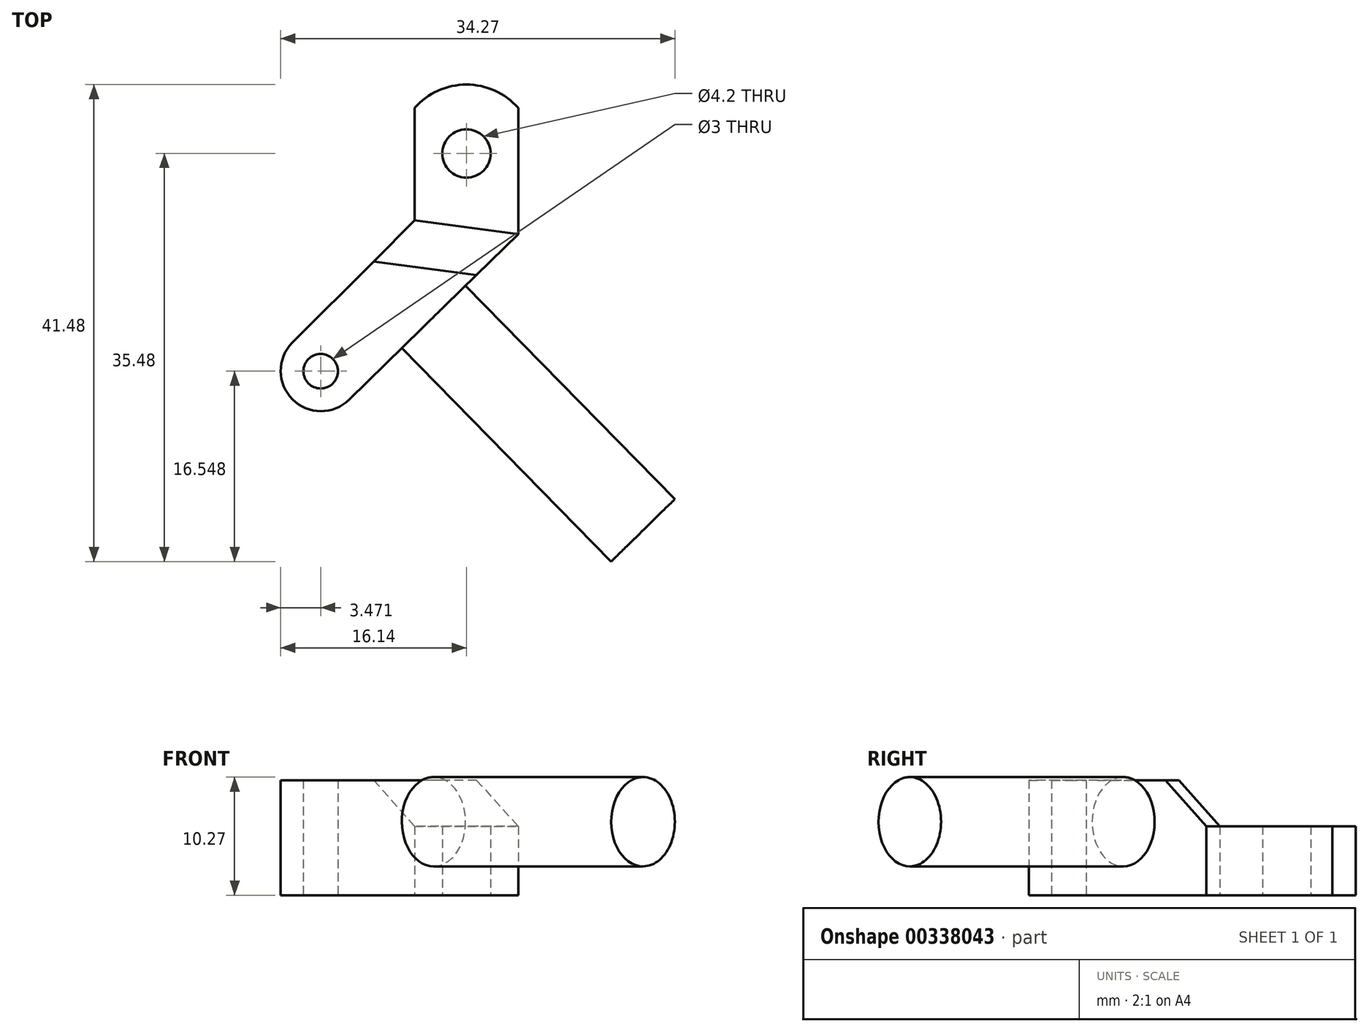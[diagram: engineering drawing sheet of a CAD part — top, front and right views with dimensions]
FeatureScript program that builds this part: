
annotation { "Feature Type Name" : "Feature", "Feature Type Description" : "" }
export const myFeature = defineFeature(function(context is Context, id is Id, definition is map)
    precondition{}
    {
        {
            var Q0;
            Q0=qCreatedBy(makeId("Top.planeOp"),FACE);
            var sketch = newSketch(context, id + "F0", { "sketchPlane" : qUnion([Q0])});
            skPoint(sketch, "E0.middle", {"position": v(0, 0) * mm});
            skCircle(sketch, "E1", {"center": v(0, 0) * mm, "radius": 2.1 * mm});
            skArc(sketch, "E2", {"start": v(4.5, 3.97) * mm, "mid": v(0, 6) * mm, "end": v(-4.5, 3.97) * mm});
            skLineSegment(sketch, "E3", {"start": v(4.5, 0) * mm, "end": v(4.5, 3.97) * mm});
            skLineSegment(sketch, "E4", {"start": v(0, 14.22) * mm, "end": v(0, -15.58) * mm, "construction": true});
            skLineSegment(sketch, "E5.MirrorCS", {"start": v(-4.5, 0) * mm, "end": v(-4.5, 3.97) * mm});
            skLineSegment(sketch, "E6", {"start": v(-4.5, 0) * mm, "end": v(-4.5, -5.81) * mm});
            skLineSegment(sketch, "E7", {"start": v(4.5, 0) * mm, "end": v(4.5, -7) * mm});
            skLineSegment(sketch, "E8", {"start": v(4.5, -7) * mm, "end": v(-10.2, -21.4) * mm});
            skCircle(sketch, "E9", {"center": v(-12.67, -18.93) * mm, "radius": 1.5 * mm});
            skLineSegment(sketch, "E10", {"start": v(-15.14, -16.46) * mm, "end": v(-4.5, -5.81) * mm});
            skArc(sketch, "E11", {"start": v(-15.14, -16.46) * mm, "mid": v(-15.12, -21.38) * mm, "end": v(-10.2, -21.4) * mm});
            skSolve(sketch);
        }
        {
            var Q0;
            Q0=makeQuery(id+"F0.imprint","IMPRINT",FACE,{"disambiguationData":[TD([[makeQuery(id+"F0.imprint","IMPRINT",EDGE,{"derivedFrom":sQuery(id+"F0.wireOp",EDGE,"E1")}),-1.0]])]});
            extrude(context, id + "F1", {"entities" : qUnion([Q0]), "depth" : 6 * mm});
        }
        {
            var Q0;
            Q0=makeQuery(id+"F1.opExtrude","SWEPT_FACE",FACE,{"disambiguationData":[OSD([sQuery(id+"F0.wireOp",EDGE,"E8")])]});
            var sketch = newSketch(context, id + "F2", { "sketchPlane" : qUnion([Q0])});
            skCircle(sketch, "E12", {"center": v(-11.98, 6.39) * mm, "radius": 3.88 * mm});
            skPoint(sketch, "E12.centerSnap0", {"position": v(-11.98, 0) * mm});
            skSolve(sketch);
        }
        {
            var Q0;
            Q0=qSketchRegion(id+"F2",true);
            extrude(context, id + "F3", {"entities" : qUnion([Q0]), "operationType" : NewBodyOperationType.ADD, "depth" : 26 * mm});
        }
        {
            var Q0;
            Q0=makeQuery(id+"F1.opExtrude","CAP_FACE",FACE,{"disambiguationData":[OSD([sQuery(id+"F0.wireOp",EDGE,"E1"),sQuery(id+"F0.wireOp",EDGE,"E2"),sQuery(id+"F0.wireOp",EDGE,"E3"),sQuery(id+"F0.wireOp",EDGE,"E5.MirrorCS"),sQuery(id+"F0.wireOp",EDGE,"E6"),sQuery(id+"F0.wireOp",EDGE,"E7"),sQuery(id+"F0.wireOp",EDGE,"fevaChrg-Coj6-oIWq-uAff-xxir51bPTQII"),sQuery(id+"F0.wireOp",EDGE,"E8"),sQuery(id+"F0.wireOp",EDGE,"KdgI6nSY-xIYV-bknZ-vAWY-uVqInj6f8gQ3"),sQuery(id+"F0.wireOp",EDGE,"E9")])],"isStart":false});
            var sketch = newSketch(context, id + "F4", { "sketchPlane" : qUnion([Q0])});
            skCircle(sketch, "E13.0", {"center": v(-12.67, -18.93) * mm, "radius": 1.5 * mm});
            skLineSegment(sketch, "E14.0", {"start": v(-15.14, -16.46) * mm, "end": v(-4.5, -5.81) * mm});
            skArc(sketch, "E15.0", {"start": v(-15.14, -16.46) * mm, "mid": v(-15.12, -21.38) * mm, "end": v(-10.2, -21.4) * mm});
            skLineSegment(sketch, "E16.0", {"start": v(-5.6, -16.9) * mm, "end": v(-10.2, -21.4) * mm});
            skLineSegment(sketch, "E17.0", {"start": v(-0.08, -11.49) * mm, "end": v(-5.6, -16.9) * mm});
            skLineSegment(sketch, "E18.0", {"start": v(4.5, -7) * mm, "end": v(-0.08, -11.49) * mm});
            skLineSegment(sketch, "E19", {"start": v(-4.5, -5.81) * mm, "end": v(4.5, -7) * mm});
            skSolve(sketch);
        }
        {
            var Q0;
            Q0=qSketchRegion(id+"F4",true);
            extrude(context, id + "F5", {"entities" : qUnion([Q0]), "operationType" : NewBodyOperationType.ADD, "depth" : (1.5 + 2.5) * mm});
        }
        {
            var Q0;
            Q0=makeQuery(id+"F5.opExtrude","CAP_EDGE",EDGE,{"disambiguationData":[OSD([sQuery(id+"F4.wireOp",EDGE,"E19")])],"isStart":false});
            var Q1;
            Q1=makeQuery(id+"FoT9Dokfan3w8GT_1.opExtrude","CAP_EDGE",EDGE,{"disambiguationData":[OSD([sQuery(id+"FRIkyxrth4iyesF_1.wireOp",EDGE,"hAYxlsMt-jx51-wO4q-qNiL-5pSk3BqyWTJ9")])],"isStart":false});
            chamfer(context, id + "F6", {"entities" : qUnion([Q0, Q1]), "width" : 4 * mm, "tangentPropagation" : true});
        }
    });
